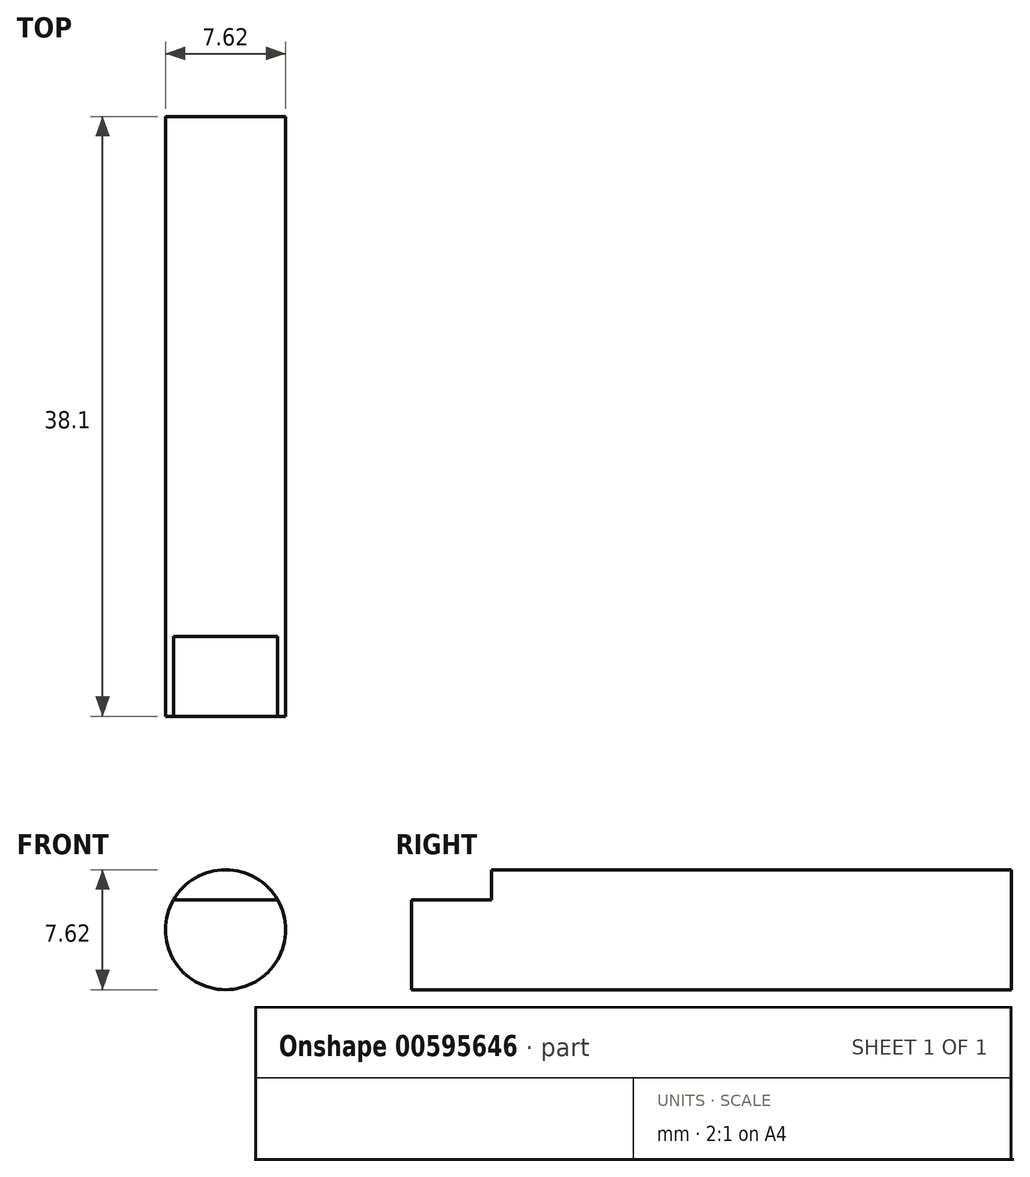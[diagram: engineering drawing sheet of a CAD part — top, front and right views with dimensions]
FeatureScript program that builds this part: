
annotation { "Feature Type Name" : "Feature", "Feature Type Description" : "" }
export const myFeature = defineFeature(function(context is Context, id is Id, definition is map)
    precondition{}
    {
        {
            var Q0;
            Q0=qCreatedBy(makeId("Front.planeOp"),FACE);
            var sketch = newSketch(context, id + "F0", { "sketchPlane" : qUnion([Q0])});
            skCircle(sketch, "E0", {"center": v(0, 0) * mm, "radius": 3.8 * mm});
            skLineSegment(sketch, "E1", {"start": v(-3.3, 1.9) * mm, "end": v(3.3, 1.9) * mm});
            skSolve(sketch);
        }
        {
            var Q0;
            Q0 = qSketchRegion(id + "F0", true);
            extrude(context, id + "F1", {"entities" : qUnion([Q0]), "oppositeDirection" : true, "depth" : 38.1 * mm, "offsetDistance" : 25.4 * mm});
        }
        {
            var Q0;
            {var subQ0=sQuery(id+"F0.wireOp",EDGE,"E1");Q0=makeQuery(id+"F0.imprint","IMPRINT",FACE,{"disambiguationData":[TD([[makeQuery(id+"F0.imprint","IMPRINT",EDGE,{"derivedFrom":subQ0}),1.0]])]});}
            extrude(context, id + "F2", {"entities" : qUnion([Q0]), "operationType" : NewBodyOperationType.REMOVE, "oppositeDirection" : true, "depth" : 5.08 * mm, "offsetDistance" : 25.4 * mm});
        }
    });
